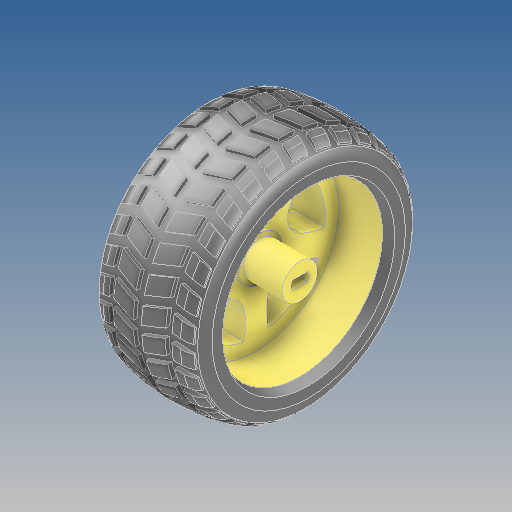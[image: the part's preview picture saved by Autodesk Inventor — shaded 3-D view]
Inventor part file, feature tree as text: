
AUTODESK INVENTOR PART (.ipt)
format: ipt  version: 2020 (Build 240168000, 168)  size: 2,428,928 bytes
history: mixed  units: in
note: dims shown in document units (in); Inventor stores cm internally (conversion verified against a paired STEP export)
features: fillet x1, imported_body x1
ambient origin geometry x8: Origin, YZ Plane, XZ Plane, XY Plane, X Axis, Y Axis, Z Axis, Center Point
bodies: Solid1 (imported_parasolid)
feature tree (2):
  fillet  "Fillet3"  [1 undecoded]
  imported_body  NMx_Import_Brep_tag  [imported B-rep: ~8 faces, bbox_mm=[0.0, 2.5, 0.0]]
note: 1 required parameter value undecoded (feature->parameter linkage not recoverable at this tier; creation-order binding heuristic only, values carry confidence <= 0.55)
